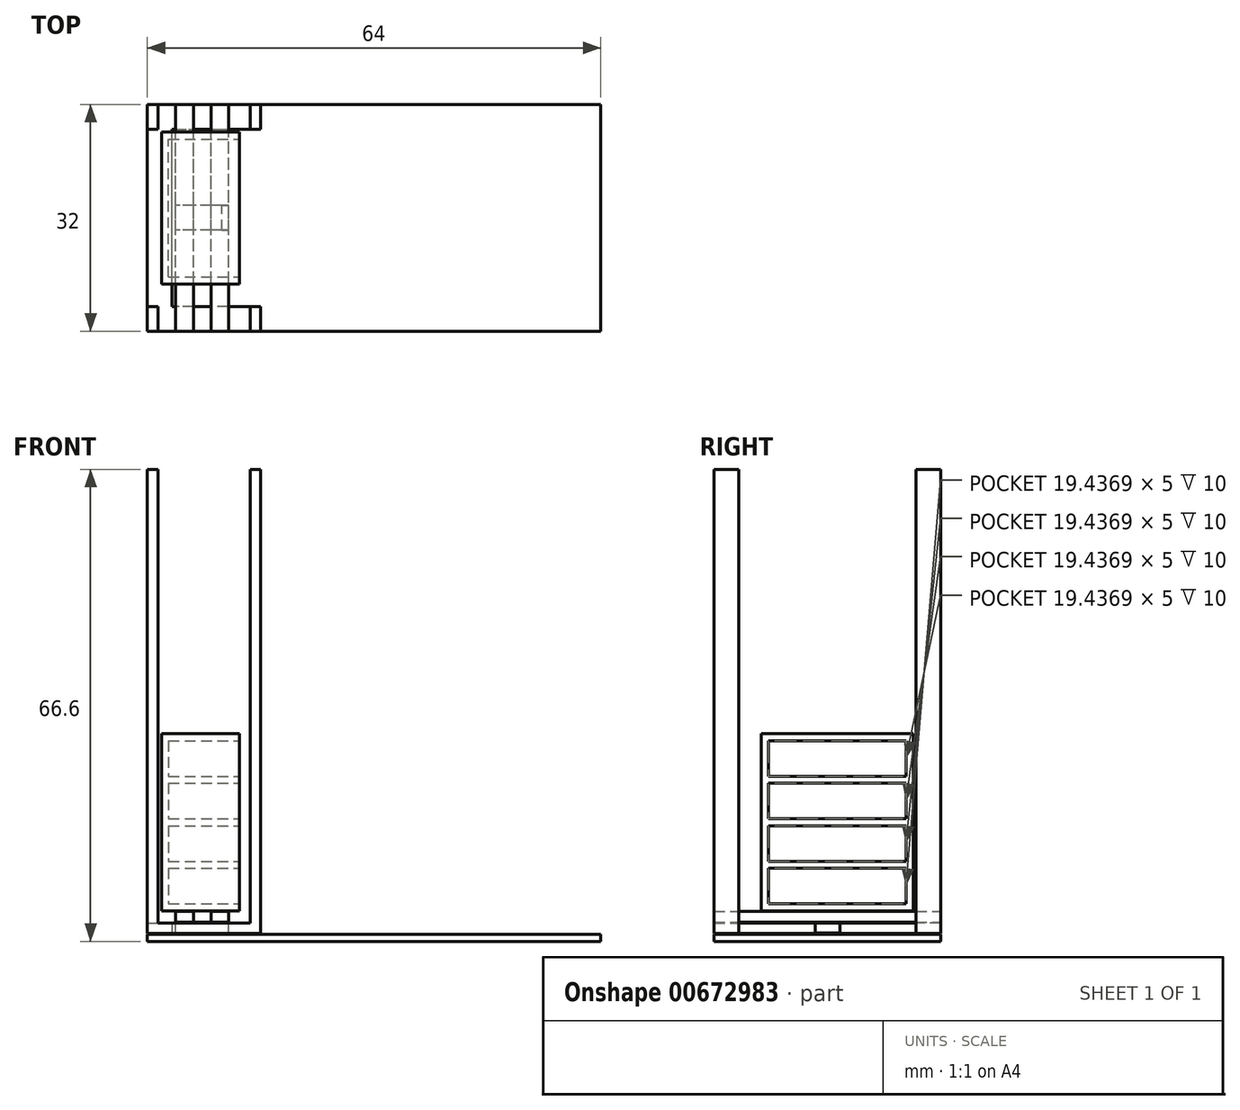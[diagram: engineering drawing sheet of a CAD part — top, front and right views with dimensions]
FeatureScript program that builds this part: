
annotation { "Feature Type Name" : "Feature", "Feature Type Description" : "" }
export const myFeature = defineFeature(function(context is Context, id is Id, definition is map)
    precondition{}
    {
        {
            var Q0;
            Q0=qCreatedBy(makeId("Top.planeOp"),FACE);
            var sketch = newSketch(context, id + "F0", { "sketchPlane" : qUnion([Q0])});
            skLineSegment(sketch, "E0.bottom", {"start": v(32, -16) * mm, "end": v(-32, -16) * mm});
            skLineSegment(sketch, "E0.top", {"start": v(32, 16) * mm, "end": v(-32, 16) * mm});
            skLineSegment(sketch, "E0.left", {"start": v(32, -16) * mm, "end": v(32, 16) * mm});
            skLineSegment(sketch, "E0.right", {"start": v(-32, -16) * mm, "end": v(-32, 16) * mm});
            skPoint(sketch, "E0.middle", {"position": v(0, 0) * mm});
            skSolve(sketch);
        }
        {
            var Q0;
            Q0 = qSketchRegion(id + "F0", true);
            extrude(context, id + "F1", {"entities" : qUnion([Q0]), "depth" : 1 * mm, "offsetDistance" : 25 * mm});
        }
        {
            var Q0;
            Q0=makeQuery(id+"F1.opExtrude","CAP_FACE",FACE,{"disambiguationData":[OSD([sQuery(id+"F0.wireOp",EDGE,"E0.bottom"),sQuery(id+"F0.wireOp",EDGE,"E0.top"),sQuery(id+"F0.wireOp",EDGE,"E0.left"),sQuery(id+"F0.wireOp",EDGE,"E0.right")])],"isStart":false});
            cPlane(context, id + "F2", {"entities" : qUnion([Q0]), "cplaneType" : CPlaneType.OFFSET, "offset" : .1 * mm, "width" : 150 * mm, "height" : 150 * mm});
        }
        {
            var Q0;
            Q0=qCreatedBy(id+"F2.planeOp",FACE);
            var sketch = newSketch(context, id + "F3", { "sketchPlane" : qUnion([Q0])});
            skLineSegment(sketch, "E1.0", {"start": v(-32, -16) * mm, "end": v(-32, 16) * mm});
            skLineSegment(sketch, "E2", {"start": v(-32, -16) * mm, "end": v(-16, -16) * mm});
            skLineSegment(sketch, "E3", {"start": v(-32, 16) * mm, "end": v(-16, 16) * mm});
            skLineSegment(sketch, "E4", {"start": v(-16, -16) * mm, "end": v(-16, -12.5) * mm});
            skLineSegment(sketch, "E5", {"start": v(-16, -12.5) * mm, "end": v(-28.5, -12.5) * mm});
            skLineSegment(sketch, "E6", {"start": v(-28.5, -12.5) * mm, "end": v(-28.5, 12.5) * mm});
            skLineSegment(sketch, "E7", {"start": v(-28.5, 12.5) * mm, "end": v(-16, 12.5) * mm});
            skLineSegment(sketch, "E8", {"start": v(-16, 12.5) * mm, "end": v(-16, 16) * mm});
            skSolve(sketch);
        }
        {
            var Q0;
            Q0 = qSketchRegion(id + "F3", true);
            extrude(context, id + "F4", {"entities" : qUnion([Q0]), "depth" : 1.5 * mm, "offsetDistance" : 25 * mm});
        }
        {
            var Q0;
            Q0=makeQuery(id+"F4.opExtrude","CAP_FACE",FACE,{"disambiguationData":[OSD([sQuery(id+"F3.wireOp",EDGE,"E1.0"),sQuery(id+"F3.wireOp",EDGE,"E2"),sQuery(id+"F3.wireOp",EDGE,"E3"),sQuery(id+"F3.wireOp",EDGE,"E4"),sQuery(id+"F3.wireOp",EDGE,"E5"),sQuery(id+"F3.wireOp",EDGE,"E6"),sQuery(id+"F3.wireOp",EDGE,"E7"),sQuery(id+"F3.wireOp",EDGE,"E8")])],"isStart":false});
            var sketch = newSketch(context, id + "F5", { "sketchPlane" : qUnion([Q0])});
            skLineSegment(sketch, "E9.bottom", {"start": v(-16, -16) * mm, "end": v(-17.5, -16) * mm});
            skLineSegment(sketch, "E9.top", {"start": v(-16, -12.5) * mm, "end": v(-17.5, -12.5) * mm});
            skLineSegment(sketch, "E9.left", {"start": v(-16, -16) * mm, "end": v(-16, -12.5) * mm});
            skLineSegment(sketch, "E9.right", {"start": v(-17.5, -16) * mm, "end": v(-17.5, -12.5) * mm});
            skLineSegment(sketch, "E10.bottom", {"start": v(-16, 12.5) * mm, "end": v(-17.5, 12.5) * mm});
            skLineSegment(sketch, "E10.top", {"start": v(-16, 16) * mm, "end": v(-17.5, 16) * mm});
            skLineSegment(sketch, "E10.left", {"start": v(-16, 12.5) * mm, "end": v(-16, 16) * mm});
            skLineSegment(sketch, "E10.right", {"start": v(-17.5, 12.5) * mm, "end": v(-17.5, 16) * mm});
            skLineSegment(sketch, "E11.bottom", {"start": v(-32, -16) * mm, "end": v(-30.5, -16) * mm});
            skLineSegment(sketch, "E11.top", {"start": v(-32, -12.5) * mm, "end": v(-30.5, -12.5) * mm});
            skLineSegment(sketch, "E11.left", {"start": v(-32, -16) * mm, "end": v(-32, -12.5) * mm});
            skLineSegment(sketch, "E11.right", {"start": v(-30.5, -16) * mm, "end": v(-30.5, -12.5) * mm});
            skLineSegment(sketch, "E12.bottom", {"start": v(-32, 16) * mm, "end": v(-30.5, 16) * mm});
            skLineSegment(sketch, "E12.top", {"start": v(-32, 12.5) * mm, "end": v(-30.5, 12.5) * mm});
            skLineSegment(sketch, "E12.left", {"start": v(-32, 16) * mm, "end": v(-32, 12.5) * mm});
            skLineSegment(sketch, "E12.right", {"start": v(-30.5, 16) * mm, "end": v(-30.5, 12.5) * mm});
            skSolve(sketch);
        }
        {
            var Q0;
            Q0 = qSketchRegion(id + "F5", true);
            extrude(context, id + "F6", {"entities" : qUnion([Q0]), "operationType" : NewBodyOperationType.ADD, "depth" : 64 * mm, "offsetDistance" : 25 * mm});
        }
        {
            var Q0;
            Q0=makeQuery(id+"F4.opExtrude","CAP_FACE",FACE,{"disambiguationData":[OSD([sQuery(id+"F3.wireOp",EDGE,"E1.0"),sQuery(id+"F3.wireOp",EDGE,"E2"),sQuery(id+"F3.wireOp",EDGE,"E3"),sQuery(id+"F3.wireOp",EDGE,"E4"),sQuery(id+"F3.wireOp",EDGE,"E5"),sQuery(id+"F3.wireOp",EDGE,"E6"),sQuery(id+"F3.wireOp",EDGE,"E7"),sQuery(id+"F3.wireOp",EDGE,"E8")])],"isStart":false});
            cPlane(context, id + "F7", {"entities" : qUnion([Q0]), "cplaneType" : CPlaneType.OFFSET, "offset" : .1 * mm, "width" : 150 * mm, "height" : 150 * mm});
        }
        {
            var Q0;
            Q0=qCreatedBy(id+"F7.planeOp",FACE);
            var sketch = newSketch(context, id + "F8", { "sketchPlane" : qUnion([Q0])});
            skLineSegment(sketch, "E13.0", {"start": v(-30.5, -16) * mm, "end": v(-17.5, -16) * mm, "construction": true});
            skLineSegment(sketch, "E14.0", {"start": v(-30.5, 16) * mm, "end": v(-17.5, 16) * mm, "construction": true});
            skLineSegment(sketch, "E15.bottom", {"start": v(-28, -16) * mm, "end": v(-25.5, -16) * mm});
            skLineSegment(sketch, "E15.top", {"start": v(-28, 16) * mm, "end": v(-25.5, 16) * mm});
            skLineSegment(sketch, "E15.left", {"start": v(-28, -16) * mm, "end": v(-28, 16) * mm});
            skLineSegment(sketch, "E15.right", {"start": v(-25.5, -16) * mm, "end": v(-25.5, 16) * mm});
            skLineSegment(sketch, "E16", {"start": v(-25.5, -16) * mm, "end": v(-23, -16) * mm, "construction": true});
            skLineSegment(sketch, "E17.bottom", {"start": v(-23, -16) * mm, "end": v(-20.5, -16) * mm});
            skLineSegment(sketch, "E17.top", {"start": v(-23, 16) * mm, "end": v(-20.5, 16) * mm});
            skLineSegment(sketch, "E17.left", {"start": v(-23, -16) * mm, "end": v(-23, 16) * mm});
            skLineSegment(sketch, "E17.right", {"start": v(-20.5, -16) * mm, "end": v(-20.5, 16) * mm});
            skSolve(sketch);
        }
        {
            var Q0;
            Q0 = qSketchRegion(id + "F8", true);
            extrude(context, id + "F9", {"entities" : qUnion([Q0]), "depth" : 1.5 * mm, "offsetDistance" : 25 * mm});
        }
        {
            var Q0;
            Q0=makeQuery(id+"F9.opExtrude","CAP_FACE",FACE,{"disambiguationData":[OSD([sQuery(id+"F8.wireOp",EDGE,"E17.bottom"),sQuery(id+"F8.wireOp",EDGE,"E17.top"),sQuery(id+"F8.wireOp",EDGE,"E17.left"),sQuery(id+"F8.wireOp",EDGE,"E17.right")])],"isStart":true});
            var sketch = newSketch(context, id + "F10", { "sketchPlane" : qUnion([Q0])});
            skPoint(sketch, "E18", {"position": v(-20.5, 0) * mm});
            skPoint(sketch, "E19.0", {"position": v(-28, 0) * mm});
            skLineSegment(sketch, "E20.bottom", {"start": v(-20.5, 1.75) * mm, "end": v(-28, 1.75) * mm});
            skLineSegment(sketch, "E20.top", {"start": v(-20.5, -1.75) * mm, "end": v(-28, -1.75) * mm});
            skLineSegment(sketch, "E20.left", {"start": v(-20.5, 1.75) * mm, "end": v(-20.5, -1.75) * mm});
            skLineSegment(sketch, "E20.right", {"start": v(-28, 1.75) * mm, "end": v(-28, -1.75) * mm});
            skSolve(sketch);
        }
        {
            var Q0;
            Q0 = qSketchRegion(id + "F10", true);
            extrude(context, id + "F11", {"entities" : qUnion([Q0]), "operationType" : NewBodyOperationType.ADD, "depth" : 1.5 * mm, "offsetDistance" : 25 * mm});
        }
        {
            var Q0;
            Q0=makeQuery(id+"F11.boolean.opBoolean","MERGE",FACE,{"derivedFrom":[makeQuery(id+"F9.opExtrude","SWEPT_FACE",FACE,{"disambiguationData":[OSD([sQuery(id+"F8.wireOp",EDGE,"E17.right")])]}),makeQuery(id+"F11.opExtrude","SWEPT_FACE",FACE,{"disambiguationData":[OSD([sQuery(id+"F10.wireOp",EDGE,"E20.left")])]})]});
            var sketch = newSketch(context, id + "F12", { "sketchPlane" : qUnion([Q0])});
            skLineSegment(sketch, "E21.bottom", {"start": v(-1.75, 2.7) * mm, "end": v(1.75, 2.7) * mm});
            skLineSegment(sketch, "E21.top", {"start": v(-1.75, 2.6) * mm, "end": v(1.75, 2.6) * mm});
            skLineSegment(sketch, "E21.left", {"start": v(-1.75, 2.7) * mm, "end": v(-1.75, 2.6) * mm});
            skLineSegment(sketch, "E21.right", {"start": v(1.75, 2.7) * mm, "end": v(1.75, 2.6) * mm});
            skSolve(sketch);
        }
        {
            var Q0;
            Q0 = qSketchRegion(id + "F12", true);
            extrude(context, id + "F13", {"entities" : qUnion([Q0]), "operationType" : NewBodyOperationType.REMOVE, "oppositeDirection" : true, "depth" : 1 * mm, "offsetDistance" : 25 * mm});
        }
        {
            var Q0;
            Q0=makeQuery(id+"F9.opExtrude","CAP_FACE",FACE,{"disambiguationData":[OSD([sQuery(id+"F8.wireOp",EDGE,"E15.bottom"),sQuery(id+"F8.wireOp",EDGE,"E15.top"),sQuery(id+"F8.wireOp",EDGE,"E15.left"),sQuery(id+"F8.wireOp",EDGE,"E15.right")])],"isStart":false});
            cPlane(context, id + "F14", {"entities" : qUnion([Q0]), "cplaneType" : CPlaneType.OFFSET, "offset" : .1 * mm, "width" : 150 * mm, "height" : 150 * mm});
        }
        {
            var Q0;
            Q0=qCreatedBy(id+"F14.planeOp",FACE);
            var sketch = newSketch(context, id + "F15", { "sketchPlane" : qUnion([Q0])});
            skLineSegment(sketch, "E22.bottom", {"start": v(-30, -9.33) * mm, "end": v(-19, -9.33) * mm});
            skLineSegment(sketch, "E22.top", {"start": v(-30, 12.1) * mm, "end": v(-19, 12.1) * mm});
            skLineSegment(sketch, "E22.left", {"start": v(-30, -9.33) * mm, "end": v(-30, 12.1) * mm});
            skLineSegment(sketch, "E22.right", {"start": v(-19, -9.33) * mm, "end": v(-19, 12.1) * mm});
            skSolve(sketch);
        }
        {
            var Q0;
            Q0 = qSketchRegion(id + "F15", true);
            extrude(context, id + "F16", {"entities" : qUnion([Q0]), "depth" : 25 * mm, "offsetDistance" : 25 * mm});
        }
        {
            var Q0;
            Q0=makeQuery(id+"F16.opExtrude","SWEPT_FACE",FACE,{"disambiguationData":[OSD([sQuery(id+"F15.wireOp",EDGE,"E22.right")])]});
            var sketch = newSketch(context, id + "F17", { "sketchPlane" : qUnion([Q0])});
            skLineSegment(sketch, "E23.bottom", {"start": v(-8.33, 28.3) * mm, "end": v(11.1, 28.3) * mm});
            skLineSegment(sketch, "E23.top", {"start": v(-8.33, 23.3) * mm, "end": v(11.1, 23.3) * mm});
            skLineSegment(sketch, "E23.left", {"start": v(-8.33, 28.3) * mm, "end": v(-8.33, 23.3) * mm});
            skLineSegment(sketch, "E23.right", {"start": v(11.1, 28.3) * mm, "end": v(11.1, 23.3) * mm});
            skLineSegment(sketch, "E24.0.1.0", {"start": v(-8.33, 22.3) * mm, "end": v(-8.33, 17.3) * mm});
            skLineSegment(sketch, "E24.0.1.1", {"start": v(-8.33, 22.3) * mm, "end": v(11.1, 22.3) * mm});
            skLineSegment(sketch, "E24.0.1.2", {"start": v(11.1, 22.3) * mm, "end": v(11.1, 17.3) * mm});
            skLineSegment(sketch, "E24.0.1.3", {"start": v(-8.33, 17.3) * mm, "end": v(11.1, 17.3) * mm});
            skLineSegment(sketch, "E24.0.2.0", {"start": v(-8.33, 16.3) * mm, "end": v(-8.33, 11.3) * mm});
            skLineSegment(sketch, "E24.0.2.1", {"start": v(-8.33, 16.3) * mm, "end": v(11.1, 16.3) * mm});
            skLineSegment(sketch, "E24.0.2.2", {"start": v(11.1, 16.3) * mm, "end": v(11.1, 11.3) * mm});
            skLineSegment(sketch, "E24.0.2.3", {"start": v(-8.33, 11.3) * mm, "end": v(11.1, 11.3) * mm});
            skLineSegment(sketch, "E24.0.3.0", {"start": v(-8.33, 10.3) * mm, "end": v(-8.33, 5.3) * mm});
            skLineSegment(sketch, "E24.0.3.1", {"start": v(-8.33, 10.3) * mm, "end": v(11.1, 10.3) * mm});
            skLineSegment(sketch, "E24.0.3.2", {"start": v(11.1, 10.3) * mm, "end": v(11.1, 5.3) * mm});
            skLineSegment(sketch, "E24.0.3.3", {"start": v(-8.33, 5.3) * mm, "end": v(11.1, 5.3) * mm});
            skLineSegment(sketch, "E24.direction1", {"start": v(-8.33, 23.3) * mm, "end": v(16.7, 23.3) * mm, "construction": true});
            skLineSegment(sketch, "E24.direction2", {"start": v(-8.33, 23.3) * mm, "end": v(-8.33, 17.3) * mm, "construction": true});
            skSolve(sketch);
        }
        {
            var Q0;
            Q0 = qSketchRegion(id + "F17", true);
            extrude(context, id + "F18", {"entities" : qUnion([Q0]), "operationType" : NewBodyOperationType.REMOVE, "oppositeDirection" : true, "depth" : 10 * mm, "offsetDistance" : 25 * mm});
        }
    });
